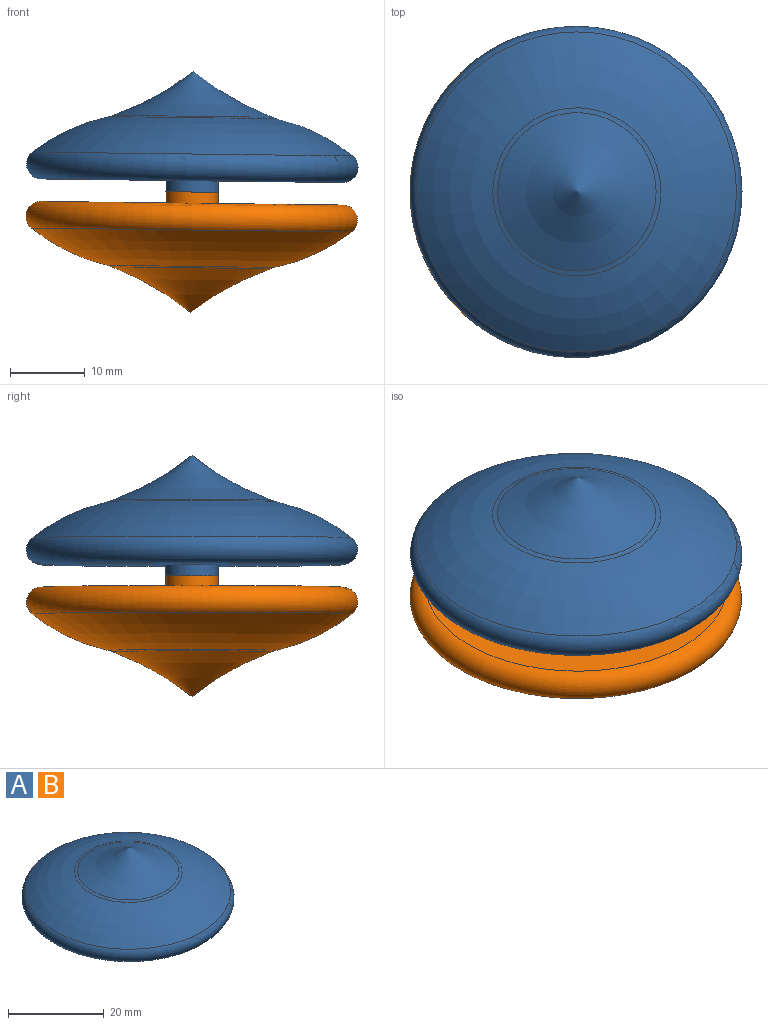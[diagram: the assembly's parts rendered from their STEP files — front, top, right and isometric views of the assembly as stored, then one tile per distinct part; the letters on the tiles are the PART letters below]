
ASSEMBLY  parts=2 mates=1
PART A: 7 faces, bbox 47.8x47.8x16.1 mm
  f0: torus R=23.77mm, axis (-0.01,0,-1), area 392.2mm2, adj f4
  f1: torus R=5.72mm, axis (-0.01,0,-1), area 1171mm2, adj f3,f4
  f2: plane 40.2x40.19mm, normal (-0.01,0,-1), area 1230.5mm2, adj f3,f5
  f3: torus R=20.1mm, axis (0.01,0,1), area 668.8mm2, adj f1,f2
  f4: torus R=12.3mm, axis (-0.01,0,-1), area 46mm2, adj f0,f1
  f5: cylinder r=3.5mm len=7.02mm, axis (0.01,0,1), area 33mm2, adj f2,f6
  f6: plane 7x7mm, normal (-0.01,0,-1), area 38.5mm2, adj f5
PART B: same geometry as A
PLACE A at identity
PLACE B rot(axis=(1,0,-0.01),180deg) t=(0.28,0,23.6)mm
MATE fastened B.f5 <-> A.f5  axis (0.01,0,1) through (-9.83,0,11.92)mm
